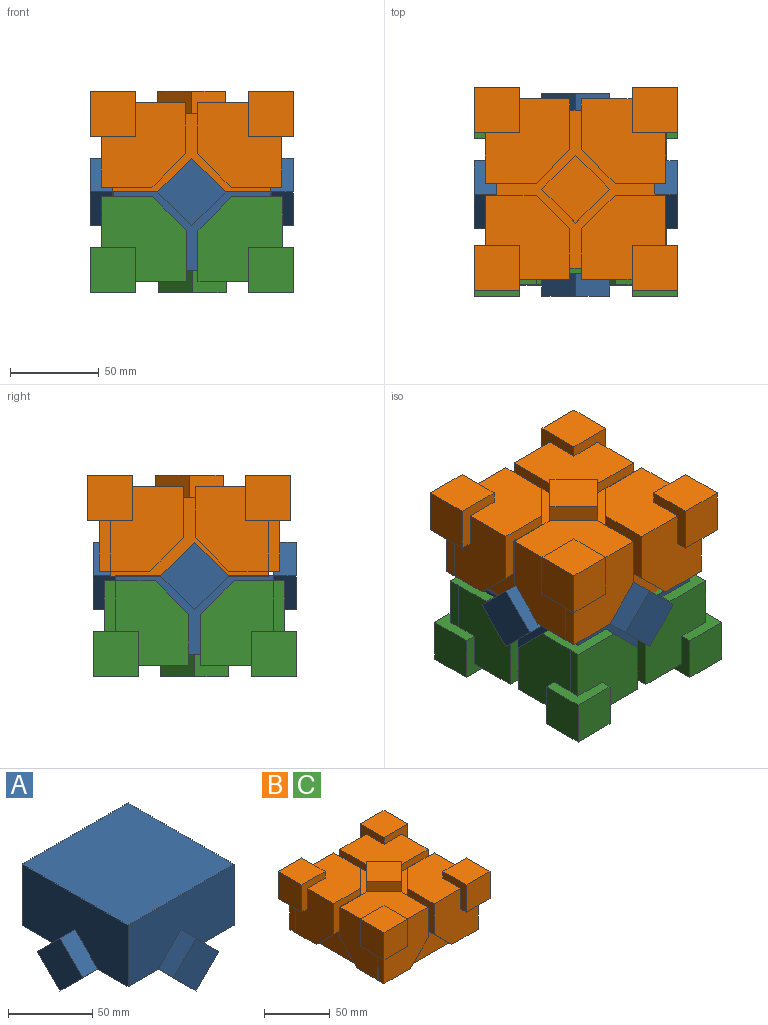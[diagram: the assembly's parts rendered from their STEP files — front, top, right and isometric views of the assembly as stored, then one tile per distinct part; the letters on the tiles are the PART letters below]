
ASSEMBLY  parts=3 mates=2
PART A: 39 faces, bbox 114.3x114.3x63.5 mm
  f0: plane 88.9x88.9mm, normal (0,0,-1), area 3104.2mm2, adj f1,f2,f3,f4,f11,f13,f14,f15
  f1: plane 88.9x44.45mm, normal (1,0,0), area 3587.4mm2, adj f0,f2,f4,f5,f35,f36
  f2: plane 88.9x44.45mm, normal (0,1,0), area 3587.4mm2, adj f0,f1,f3,f5,f23,f24
  f3: plane 88.9x44.45mm, normal (-1,0,0), area 3587.4mm2, adj f0,f2,f4,f5,f29,f30
  f4: plane 88.9x44.45mm, normal (0,-1,0), area 3587.4mm2, adj f0,f1,f3,f5,f8,f9
  f5: plane 88.9x88.9mm, normal (0,0,1), area 7903.2mm2, adj f1,f2,f3,f4
  f6: plane 19.08x19.08mm, normal (-0.71,0,-0.71), area 342.7mm2, adj f7,f9,f10,f11
  f7: plane 19.08x19.08mm, normal (0.71,0,-0.71), area 342.7mm2, adj f6,f8,f10,f11
  f8: plane 19.08x19.08mm, normal (0.71,0,0.71), area 342.7mm2, adj f4,f7,f9,f10
  f9: plane 19.08x19.08mm, normal (-0.71,0,0.71), area 342.7mm2, adj f4,f6,f8,f10
  f10: plane 38.17x38.17mm, normal (0,-1,0), area 728.3mm2, adj f6,f7,f8,f9
  f11: plane 38.17x19.08mm, normal (0,1,0), area 364.2mm2, adj f0,f6,f7,f12
  f12: plane 9.43x2.54mm, normal (0,0,1), area 24mm2, adj f11,f18,f19,f20
  f13: plane 68.58x34.29mm, normal (-1,0,0), area 2351.6mm2, adj f0,f14,f16,f17
  f14: plane 68.58x34.29mm, normal (0,-1,0), area 2351.6mm2, adj f0,f13,f15,f17
  f15: plane 68.58x34.29mm, normal (1,0,0), area 2351.6mm2, adj f0,f14,f16,f17
  f16: plane 68.58x34.29mm, normal (0,1,0), area 2329.4mm2, adj f0,f13,f15,f17,f18,f19
  f17: plane 68.58x68.58mm, normal (0,0,-1), area 4703.2mm2, adj f13,f14,f15,f16
  f18: plane 12.7x4.71mm, normal (-0.71,0,-0.71), area 84.7mm2, adj f0,f12,f16,f19,f20
  f19: plane 12.7x4.71mm, normal (0.71,0,-0.71), area 84.7mm2, adj f0,f12,f16,f18,f20
  f20: plane 9.43x4.71mm, normal (0,1,0), area 22.2mm2, adj f12,f18,f19
  f21: plane 38.17x19.08mm, normal (0,-1,0), area 364.2mm2, adj f0,f22,f25
  f22: plane 19.08x19.08mm, normal (-0.71,0,-0.71), area 342.7mm2, adj f21,f23,f25,f26
  f23: plane 19.08x19.08mm, normal (-0.71,0,0.71), area 342.7mm2, adj f2,f22,f24,f26
  f24: plane 19.08x19.08mm, normal (0.71,0,0.71), area 342.7mm2, adj f2,f23,f25,f26
  f25: plane 19.08x19.08mm, normal (0.71,0,-0.71), area 342.7mm2, adj f21,f22,f24,f26
  f26: plane 38.17x38.17mm, normal (0,1,0), area 728.3mm2, adj f22,f23,f24,f25
  f27: plane 19.08x19.08mm, normal (0,0.71,-0.71), area 342.7mm2, adj f28,f30,f31,f32
  f28: plane 19.08x19.08mm, normal (0,-0.71,-0.71), area 342.7mm2, adj f27,f29,f31,f32
  f29: plane 19.08x19.08mm, normal (0,-0.71,0.71), area 342.7mm2, adj f3,f28,f30,f31
  f30: plane 19.08x19.08mm, normal (0,0.71,0.71), area 342.7mm2, adj f3,f27,f29,f31
  f31: plane 38.17x38.17mm, normal (-1,0,0), area 728.3mm2, adj f27,f28,f29,f30
  f32: plane 38.17x19.08mm, normal (1,0,0), area 364.2mm2, adj f0,f27,f28
  f33: plane 38.17x19.08mm, normal (-1,0,0), area 364.2mm2, adj f0,f34,f37
  f34: plane 19.08x19.08mm, normal (0,0.71,-0.71), area 342.7mm2, adj f33,f35,f37,f38
  f35: plane 19.08x19.08mm, normal (0,0.71,0.71), area 342.7mm2, adj f1,f34,f36,f38
  f36: plane 19.08x19.08mm, normal (0,-0.71,0.71), area 342.7mm2, adj f1,f35,f37,f38
  f37: plane 19.08x19.08mm, normal (0,-0.71,-0.71), area 342.7mm2, adj f33,f34,f36,f38
  f38: plane 38.17x38.17mm, normal (1,0,0), area 728.3mm2, adj f34,f35,f36,f37
PART B: 80 faces, bbox 114.3x114.3x57.2 mm
  f0: plane 47.5x47.5mm, normal (0,0,1), area 1714.1mm2, adj f5,f6,f21,f43,f49,f64,f66
  f1: plane 47.63x47.5mm, normal (0,0,1), area 1718.9mm2, adj f14,f17,f18,f39,f48,f57,f61
  f2: plane 47.63x47.5mm, normal (0,0,1), area 1718.9mm2, adj f4,f28,f29,f40,f47,f75,f79
  f3: plane 28.58x0.13mm, normal (0,-1,0), area 3.6mm2, adj f32,f33,f46,f71
  f4: plane 47.63x47.63mm, normal (0,1,0), area 1723.8mm2, adj f2,f28,f29,f30,f31,f75,f76
  f5: plane 47.63x47.63mm, normal (0,-1,0), area 1721.4mm2, adj f0,f19,f20,f21,f22,f62,f66
  f6: plane 47.63x41.15mm, normal (-1,0,0), area 1537.5mm2, adj f0,f9,f19,f42,f43,f62,f64
  f7: plane 88.9x88.9mm, normal (0,0,1), area 1109.7mm2, adj f8,f10,f11,f12,f14,f21,f28,f35
  f8: plane 88.9x44.45mm, normal (-1,0,0), area 915.3mm2, adj f7,f11,f12,f13,f19,f32,f42,f43
  f9: plane 28.58x0.13mm, normal (0,1,0), area 3.6mm2, adj f6,f19,f22,f62
  f10: plane 88.9x44.45mm, normal (1,0,0), area 915.3mm2, adj f7,f11,f12,f13,f16,f30,f38,f39
  f11: plane 88.9x44.45mm, normal (0,1,0), area 912.5mm2, adj f7,f8,f10,f13,f28,f30,f31,f32
  f12: plane 88.9x44.45mm, normal (0,-1,0), area 912.5mm2, adj f7,f8,f10,f13,f14,f15,f16,f19
  f13: plane 88.9x88.9mm, normal (0,0,-1), area 3200mm2, adj f8,f10,f11,f12,f23,f24,f25,f26
  f14: plane 28.58x28.58mm, normal (-1,0,0), area 322.6mm2, adj f1,f7,f12,f15,f18,f48
  f15: plane 19.05x19.05mm, normal (-0.71,0,-0.71), area 171.1mm2, adj f12,f14,f16,f18
  f16: plane 28.58x28.58mm, normal (0,0,-1), area 322.6mm2, adj f10,f12,f15,f17,f18,f38
  f17: plane 47.63x47.5mm, normal (1,0,0), area 1718.9mm2, adj f1,f16,f18,f38,f39,f58,f61
  f18: plane 47.63x47.63mm, normal (0,-1,0), area 1723.8mm2, adj f1,f14,f15,f16,f17,f57,f58
  f19: plane 28.58x28.58mm, normal (0,0,-1), area 322.6mm2, adj f5,f6,f8,f9,f12,f20,f22,f42
  f20: plane 19.05x19.05mm, normal (0.71,0,-0.71), area 171.1mm2, adj f5,f12,f19,f21
  f21: plane 28.58x28.58mm, normal (1,0,0), area 322.6mm2, adj f0,f5,f7,f12,f20,f49
  f22: plane 28.58x6.35mm, normal (-1,0,0), area 181.5mm2, adj f5,f9,f19,f62
  f23: plane 68.58x34.29mm, normal (0,1,0), area 2351.6mm2, adj f13,f24,f26,f27
  f24: plane 68.58x34.29mm, normal (-1,0,0), area 2351.6mm2, adj f13,f23,f25,f27
  f25: plane 68.58x34.29mm, normal (0,-1,0), area 2351.6mm2, adj f13,f24,f26,f27
  f26: plane 68.58x34.29mm, normal (1,0,0), area 2351.6mm2, adj f13,f23,f25,f27
  f27: plane 68.58x68.58mm, normal (0,0,-1), area 4703.2mm2, adj f23,f24,f25,f26
  f28: plane 28.58x28.58mm, normal (-1,0,0), area 322.6mm2, adj f2,f4,f7,f11,f31,f47
  f29: plane 47.63x47.5mm, normal (1,0,0), area 1718.9mm2, adj f2,f4,f30,f40,f41,f76,f79
  f30: plane 28.58x28.58mm, normal (0,0,-1), area 322.6mm2, adj f4,f10,f11,f29,f31,f41
  f31: plane 19.05x19.05mm, normal (-0.71,0,-0.71), area 171.1mm2, adj f4,f11,f28,f30
  f32: plane 28.58x28.58mm, normal (0,0,-1), area 322.6mm2, adj f3,f8,f11,f33,f36,f37,f44,f46
  f33: plane 28.58x6.35mm, normal (-1,0,0), area 181.5mm2, adj f3,f32,f37,f71
  f34: plane 47.5x47.5mm, normal (0,0,1), area 1714.1mm2, adj f35,f37,f45,f46,f50,f72,f73
  f35: plane 28.58x28.58mm, normal (1,0,0), area 322.6mm2, adj f7,f11,f34,f36,f37,f50
  f36: plane 19.05x19.05mm, normal (0.71,0,-0.71), area 171.1mm2, adj f11,f32,f35,f37
  f37: plane 47.63x47.63mm, normal (0,1,0), area 1721.4mm2, adj f32,f33,f34,f35,f36,f71,f73
  f38: plane 19.05x18.92mm, normal (0,0.71,-0.7), area 170.5mm2, adj f10,f16,f17,f39
  f39: plane 28.58x28.58mm, normal (0,1,0), area 322.6mm2, adj f1,f7,f10,f17,f38,f48
  f40: plane 28.58x28.58mm, normal (0,-1,0), area 322.6mm2, adj f2,f7,f10,f29,f41,f47
  f41: plane 19.05x18.92mm, normal (0,-0.71,-0.7), area 170.5mm2, adj f10,f29,f30,f40
  f42: plane 19.05x18.92mm, normal (0,0.71,-0.7), area 170.5mm2, adj f6,f8,f19,f43
  f43: plane 28.58x28.58mm, normal (0,1,0), area 322.6mm2, adj f0,f6,f7,f8,f42,f49
  f44: plane 19.05x18.92mm, normal (0,-0.71,-0.7), area 170.5mm2, adj f8,f32,f45,f46
  f45: plane 28.58x28.58mm, normal (0,-1,0), area 322.6mm2, adj f7,f8,f34,f44,f46,f50
  f46: plane 47.63x41.15mm, normal (-1,0,0), area 1537.5mm2, adj f3,f32,f34,f44,f45,f71,f72
  f47: plane 19.05x18.92mm, normal (-0.7,-0.71,0), area 170.5mm2, adj f2,f7,f28,f40
  f48: plane 19.05x18.92mm, normal (-0.7,0.71,0), area 170.5mm2, adj f1,f7,f14,f39
  f49: plane 18.92x18.92mm, normal (0.71,0.71,0), area 169.9mm2, adj f0,f7,f21,f43
  f50: plane 18.92x18.92mm, normal (0.71,-0.71,0), area 169.9mm2, adj f7,f34,f35,f45
  f51: plane 19.09x19.09mm, normal (0.71,0.71,0), area 342.9mm2, adj f7,f52,f54,f55
  f52: plane 19.09x19.09mm, normal (-0.71,0.71,0), area 342.9mm2, adj f7,f51,f53,f55
  f53: plane 19.09x19.09mm, normal (-0.71,-0.71,0), area 342.9mm2, adj f7,f52,f54,f55
  f54: plane 19.09x19.09mm, normal (0.71,-0.71,0), area 342.9mm2, adj f7,f51,f53,f55
  f55: plane 38.18x38.18mm, normal (0,0,1), area 729mm2, adj f51,f52,f53,f54
  f56: plane 25.4x25.4mm, normal (0,0,1), area 645.2mm2, adj f57,f59,f60,f61
  f57: plane 25.4x25.4mm, normal (-1,0,0), area 282.3mm2, adj f1,f18,f56,f58,f60,f61
  f58: plane 25.4x25.4mm, normal (0,0,-1), area 282.3mm2, adj f17,f18,f57,f59,f60,f61
  f59: plane 25.4x25.4mm, normal (1,0,0), area 645.2mm2, adj f56,f58,f60,f61
  f60: plane 25.4x25.4mm, normal (0,-1,0), area 645.2mm2, adj f56,f57,f58,f59
  f61: plane 25.4x25.4mm, normal (0,1,0), area 282.3mm2, adj f1,f17,f56,f57,f58,f59
  f62: plane 25.4x25.4mm, normal (0,0,-1), area 281.4mm2, adj f5,f6,f9,f22,f64,f65,f66,f67
  f63: plane 25.4x25.4mm, normal (0,0,1), area 645.2mm2, adj f64,f65,f66,f67
  f64: plane 25.4x25.4mm, normal (0,1,0), area 282.3mm2, adj f0,f6,f62,f63,f65,f66
  f65: plane 25.4x25.4mm, normal (-1,0,0), area 645.2mm2, adj f62,f63,f64,f67
  f66: plane 25.4x25.4mm, normal (1,0,0), area 282.3mm2, adj f0,f5,f62,f63,f64,f67
  f67: plane 25.4x25.4mm, normal (0,-1,0), area 645.2mm2, adj f62,f63,f65,f66
  f68: plane 25.4x25.4mm, normal (0,0,1), area 645.2mm2, adj f69,f70,f72,f73
  f69: plane 25.4x25.4mm, normal (0,1,0), area 645.2mm2, adj f68,f70,f71,f73
  f70: plane 25.4x25.4mm, normal (-1,0,0), area 645.2mm2, adj f68,f69,f71,f72
  f71: plane 25.4x25.4mm, normal (0,0,-1), area 281.4mm2, adj f3,f33,f37,f46,f69,f70,f72,f73
  f72: plane 25.4x25.4mm, normal (0,-1,0), area 282.3mm2, adj f34,f46,f68,f70,f71,f73
  f73: plane 25.4x25.4mm, normal (1,0,0), area 282.3mm2, adj f34,f37,f68,f69,f71,f72
  f74: plane 25.4x25.4mm, normal (0,0,1), area 645.2mm2, adj f75,f77,f78,f79
  f75: plane 25.4x25.4mm, normal (-1,0,0), area 282.3mm2, adj f2,f4,f74,f76,f78,f79
  f76: plane 25.4x25.4mm, normal (0,0,-1), area 282.3mm2, adj f4,f29,f75,f77,f78,f79
  f77: plane 25.4x25.4mm, normal (1,0,0), area 645.2mm2, adj f74,f76,f78,f79
  f78: plane 25.4x25.4mm, normal (0,1,0), area 645.2mm2, adj f74,f75,f76,f77
  f79: plane 25.4x25.4mm, normal (0,-1,0), area 282.3mm2, adj f2,f29,f74,f75,f76,f77
PART C: same geometry as B
PLACE A rot(axis=(0.71,-0.71,0),180deg) t=(0,-3.05,-43.94)mm
PLACE B at identity
PLACE C rot(axis=(1,0,0),180deg) t=(0.38,-3.03,1.01)mm
MATE parallel C.f27 <-> B.f27  axis (0,0,1) through (0.38,-3.03,-33.28)mm
MATE parallel A.f0 <-> B.f13  axis (0,0,1) through (-34.29,31.24,0.51)mm
